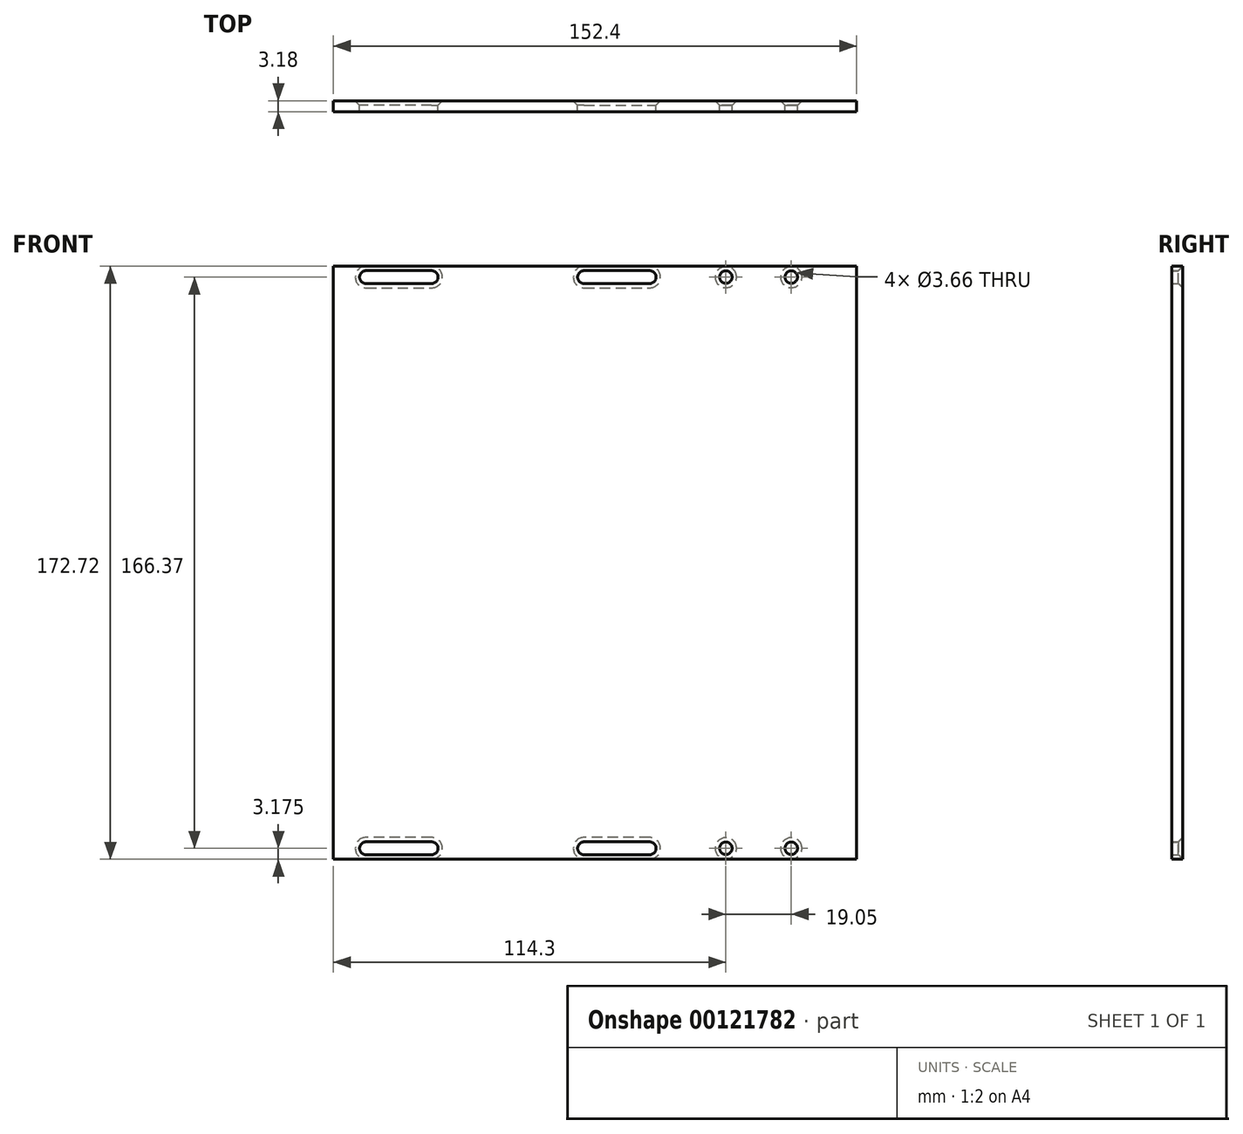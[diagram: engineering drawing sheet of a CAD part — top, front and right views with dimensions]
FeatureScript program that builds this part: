
annotation { "Feature Type Name" : "Feature", "Feature Type Description" : "" }
export const myFeature = defineFeature(function(context is Context, id is Id, definition is map)
    precondition{}
    {
        {
            var Q0;
            Q0=qCreatedBy(makeId("Front.planeOp"),FACE);
            var sketch = newSketch(context, id + "F0", { "sketchPlane" : qUnion([Q0])});
            skLineSegment(sketch, "E0.bottom", {"start": v(76.2, -86.36) * mm, "end": v(-76.2, -86.36) * mm});
            skLineSegment(sketch, "E0.top", {"start": v(76.2, 86.36) * mm, "end": v(-76.2, 86.36) * mm});
            skLineSegment(sketch, "E0.left", {"start": v(76.2, -86.36) * mm, "end": v(76.2, 86.36) * mm});
            skLineSegment(sketch, "E0.right", {"start": v(-76.2, -86.36) * mm, "end": v(-76.2, 86.36) * mm});
            skPoint(sketch, "E0.middle", {"position": v(0, 0) * mm});
            skArc(sketch, "E1", {"start": v(-66.67, -81.3) * mm, "mid": v(-68.57, -83.19) * mm, "end": v(-66.67, -85.08) * mm});
            skArc(sketch, "E2", {"start": v(-47.62, -85.08) * mm, "mid": v(-45.73, -83.19) * mm, "end": v(-47.62, -81.3) * mm});
            skLineSegment(sketch, "E3", {"start": v(-66.67, -81.3) * mm, "end": v(-47.62, -81.3) * mm});
            skLineSegment(sketch, "E4", {"start": v(-47.62, -85.08) * mm, "end": v(-66.67, -85.08) * mm});
            skArc(sketch, "E5.MirrorCS", {"start": v(-47.62, 85.08) * mm, "mid": v(-45.73, 83.19) * mm, "end": v(-47.62, 81.3) * mm});
            skLineSegment(sketch, "E6.MirrorCS", {"start": v(-66.67, 81.3) * mm, "end": v(-47.62, 81.3) * mm});
            skLineSegment(sketch, "E7.MirrorCS", {"start": v(-47.62, 85.08) * mm, "end": v(-66.67, 85.08) * mm});
            skArc(sketch, "E8.MirrorCS", {"start": v(-66.67, 81.3) * mm, "mid": v(-68.57, 83.19) * mm, "end": v(-66.67, 85.08) * mm});
            skLineSegment(sketch, "E9", {"start": v(-25.4, 86.36) * mm, "end": v(-25.4, -120.08) * mm, "construction": true});
            skArc(sketch, "E10.MirrorCS", {"start": v(-3.17, -85.08) * mm, "mid": v(-5.07, -83.19) * mm, "end": v(-3.17, -81.3) * mm});
            skLineSegment(sketch, "E11.MirrorCS", {"start": v(-3.17, -85.08) * mm, "end": v(15.88, -85.08) * mm});
            skArc(sketch, "E12.MirrorCS", {"start": v(15.88, -81.3) * mm, "mid": v(17.77, -83.19) * mm, "end": v(15.88, -85.08) * mm});
            skLineSegment(sketch, "E13.MirrorCS", {"start": v(-3.18, 85.08) * mm, "end": v(15.87, 85.08) * mm});
            skLineSegment(sketch, "E14.MirrorCS", {"start": v(15.88, -81.3) * mm, "end": v(-3.17, -81.3) * mm});
            skArc(sketch, "E15.MirrorCS", {"start": v(15.87, 81.3) * mm, "mid": v(17.77, 83.19) * mm, "end": v(15.87, 85.08) * mm});
            skLineSegment(sketch, "E16.MirrorCS", {"start": v(-25.4, 59.18) * mm, "end": v(-25.4, 86.36) * mm, "construction": true});
            skLineSegment(sketch, "E17.MirrorCS", {"start": v(15.87, 81.3) * mm, "end": v(-3.18, 81.3) * mm});
            skPoint(sketch, "E18.MirrorCS.end.orphan", {"position": v(-66.67, 77.5) * mm});
            skPoint(sketch, "E18.MirrorCS.start.orphan", {"position": v(-66.67, 81.3) * mm});
            skPoint(sketch, "E19.trimOffspring.end.orphan", {"position": v(-25.4, 282.67) * mm});
            skPoint(sketch, "E19.trimOffspring.start.orphan", {"position": v(-25.4, 103.4) * mm});
            skArc(sketch, "E20.MirrorCS", {"start": v(-3.18, 85.08) * mm, "mid": v(-5.07, 83.19) * mm, "end": v(-3.18, 81.3) * mm});
            skPoint(sketch, "E21.MirrorCS.end.orphan", {"position": v(15.87, 85.08) * mm});
            skPoint(sketch, "E21.MirrorCS.start.orphan", {"position": v(15.87, 81.3) * mm});
            skCircle(sketch, "E22", {"center": v(38.1, -83.19) * mm, "radius": 1.83 * mm});
            skCircle(sketch, "E23", {"center": v(57.15, -83.19) * mm, "radius": 1.83 * mm});
            skCircle(sketch, "E24", {"center": v(38.1, 83.19) * mm, "radius": 1.83 * mm});
            skCircle(sketch, "E25", {"center": v(57.15, 83.19) * mm, "radius": 1.83 * mm});
            skPoint(sketch, "E26.MirrorCS.end.orphan", {"position": v(47.62, -81.3) * mm});
            skPoint(sketch, "E26.MirrorCS.start.orphan", {"position": v(47.62, -85.08) * mm});
            skPoint(sketch, "E27.MirrorCS.end.orphan", {"position": v(66.67, -85.08) * mm});
            skPoint(sketch, "E27.MirrorCS.start.orphan", {"position": v(66.67, -81.3) * mm});
            skPoint(sketch, "E28.MirrorCS.end.orphan", {"position": v(66.67, 85.08) * mm});
            skPoint(sketch, "E28.MirrorCS.start.orphan", {"position": v(66.67, 81.3) * mm});
            skPoint(sketch, "E29.MirrorCS.end.orphan", {"position": v(47.62, 81.3) * mm});
            skPoint(sketch, "E29.MirrorCS.start.orphan", {"position": v(47.62, 85.08) * mm});
            skPoint(sketch, "E30.end.orphan", {"position": v(-57.15, -81.3) * mm});
            skPoint(sketch, "E30.start.orphan", {"position": v(-57.15, 81.3) * mm});
            skSolve(sketch);
        }
        {
            var Q0;
            Q0 = qSketchRegion(id + "F0", true);
            extrude(context, id + "F1", {"entities" : qUnion([Q0]), "depth" : 3.17 * mm});
        }
        {
            var Q0;
            Q0=makeQuery(id+"F1.opExtrude","CAP_EDGE",EDGE,{"disambiguationData":[OSD([sQuery(id+"F0.wireOp",EDGE,"E25")])],"isStart":true});
            var Q1;
            Q1=makeQuery(id+"F1.opExtrude","CAP_EDGE",EDGE,{"disambiguationData":[OSD([sQuery(id+"F0.wireOp",EDGE,"E24")])],"isStart":true});
            var Q2;
            Q2=makeQuery(id+"F1.opExtrude","CAP_EDGE",EDGE,{"disambiguationData":[OSD([sQuery(id+"F0.wireOp",EDGE,"E15.MirrorCS")])],"isStart":true});
            var Q3;
            Q3=makeQuery(id+"F1.opExtrude","CAP_EDGE",EDGE,{"disambiguationData":[OSD([sQuery(id+"F0.wireOp",EDGE,"E13.MirrorCS")])],"isStart":true});
            var Q4;
            Q4=makeQuery(id+"F1.opExtrude","CAP_EDGE",EDGE,{"disambiguationData":[OSD([sQuery(id+"F0.wireOp",EDGE,"E20.MirrorCS")])],"isStart":true});
            var Q5;
            Q5=makeQuery(id+"F1.opExtrude","CAP_EDGE",EDGE,{"disambiguationData":[OSD([sQuery(id+"F0.wireOp",EDGE,"E17.MirrorCS")])],"isStart":true});
            var Q6;
            Q6=makeQuery(id+"F1.opExtrude","CAP_EDGE",EDGE,{"disambiguationData":[OSD([sQuery(id+"F0.wireOp",EDGE,"E5.MirrorCS")])],"isStart":true});
            var Q7;
            Q7=makeQuery(id+"F1.opExtrude","CAP_EDGE",EDGE,{"disambiguationData":[OSD([sQuery(id+"F0.wireOp",EDGE,"E7.MirrorCS")])],"isStart":true});
            var Q8;
            Q8=makeQuery(id+"F1.opExtrude","CAP_EDGE",EDGE,{"disambiguationData":[OSD([sQuery(id+"F0.wireOp",EDGE,"E6.MirrorCS")])],"isStart":true});
            var Q9;
            Q9=makeQuery(id+"F1.opExtrude","CAP_EDGE",EDGE,{"disambiguationData":[OSD([sQuery(id+"F0.wireOp",EDGE,"E8.MirrorCS")])],"isStart":true});
            var Q10;
            Q10=makeQuery(id+"F1.opExtrude","CAP_EDGE",EDGE,{"disambiguationData":[OSD([sQuery(id+"F0.wireOp",EDGE,"E3")])],"isStart":true});
            var Q11;
            Q11=makeQuery(id+"F1.opExtrude","CAP_EDGE",EDGE,{"disambiguationData":[OSD([sQuery(id+"F0.wireOp",EDGE,"E2")])],"isStart":true});
            var Q12;
            Q12=makeQuery(id+"F1.opExtrude","CAP_EDGE",EDGE,{"disambiguationData":[OSD([sQuery(id+"F0.wireOp",EDGE,"E4")])],"isStart":true});
            var Q13;
            Q13=makeQuery(id+"F1.opExtrude","CAP_EDGE",EDGE,{"disambiguationData":[OSD([sQuery(id+"F0.wireOp",EDGE,"E1")])],"isStart":true});
            var Q14;
            Q14=makeQuery(id+"F1.opExtrude","CAP_EDGE",EDGE,{"disambiguationData":[OSD([sQuery(id+"F0.wireOp",EDGE,"E10.MirrorCS")])],"isStart":true});
            var Q15;
            Q15=makeQuery(id+"F1.opExtrude","CAP_EDGE",EDGE,{"disambiguationData":[OSD([sQuery(id+"F0.wireOp",EDGE,"E14.MirrorCS")])],"isStart":true});
            var Q16;
            Q16=makeQuery(id+"F1.opExtrude","CAP_EDGE",EDGE,{"disambiguationData":[OSD([sQuery(id+"F0.wireOp",EDGE,"E12.MirrorCS")])],"isStart":true});
            var Q17;
            Q17=makeQuery(id+"F1.opExtrude","CAP_EDGE",EDGE,{"disambiguationData":[OSD([sQuery(id+"F0.wireOp",EDGE,"E11.MirrorCS")])],"isStart":true});
            var Q18;
            Q18=makeQuery(id+"F1.opExtrude","CAP_EDGE",EDGE,{"disambiguationData":[OSD([sQuery(id+"F0.wireOp",EDGE,"E22")])],"isStart":true});
            var Q19;
            Q19=makeQuery(id+"F1.opExtrude","CAP_EDGE",EDGE,{"disambiguationData":[OSD([sQuery(id+"F0.wireOp",EDGE,"E23")])],"isStart":true});
            chamfer(context, id + "F2", {"entities" : qUnion([Q0, Q1, Q2, Q3, Q4, Q5, Q6, Q7, Q8, Q9, Q10, Q11, Q12, Q13, Q14, Q15, Q16, Q17, Q18, Q19]), "width" : 1.27 * mm, "tangentPropagation" : true});
        }
    });
